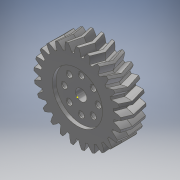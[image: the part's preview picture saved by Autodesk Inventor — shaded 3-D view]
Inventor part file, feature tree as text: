
AUTODESK INVENTOR PART (.ipt)
format: ipt  version: 2019 (Build 230136000, 136)  size: 762,368 bytes
history: native  units: mm (DEFAULTED — no unit token found)
features: sketch x7, extrude x4, plane x3, other x3, mirror x1, hole x1, chamfer x1
ambient origin geometry x8: Origin, YZ Plane, XZ Plane, XY Plane, X Axis, Y Axis, Z Axis, Center Point
bodies: Solid1 (feature_tree)
feature tree (20):
  extrude  "Extrusion1"  Depth=5.0mm TaperAngle=0.0deg
  plane  "Work Plane2"
  plane  "Work Plane8"
  plane  "Work Plane9"
  other  "Spur Gear"
  mirror  "Mirror1"
  extrude  "Extrusion13"  Depth=10.0mm TaperAngle=0.0deg
  sketch  "Sketch21"  dims[d39=0.0mm d41=0.0mm]
  extrude  "Extrusion15"  Depth=1.256637mm TaperAngle=0.0deg
  extrude  "Extrusion16"  TaperAngle=0.0deg  [1 undecoded]
  hole  "Hole4"  [1 undecoded]
  chamfer  "Chamfer2"  [1 undecoded]
  sketch  "Sketch1"  dims[d0=34.756617mm d1=5.0mm d2=0.0mm]
  sketch  "Sketch2"  dims[d3=32.258065mm d4=10.0mm d5=0.0mm]
  other  "Srf1"
  sketch  "Sketch19"  dims[d16=40.0mm d17=0.0mm d34=1.256637mm]
  sketch  "Sketch22"  dims[d43=40.0mm d46=40.0mm d47=0.0mm d48=0.0mm]
  sketch  "Sketch23"  dims[d126=4.5mm]
  sketch  "Sketch24"  dims[d127=10.0mm d128=0.0mm d132=20.0mm d133=1.5mm d134=0.0mm d135=18.0mm d136=5.0mm d137=0.0mm d138=13.5mm d139=80.0mm d141=360.0deg d143=2.5mm d144=6.0mm d145=4.0mm d146=3.0mm d147=90.0deg d148=10.0mm d149=0.0mm d150=1.5mm d151=4.0mm d152=45.0deg]
  other  "Pitch Diameter"
note: 3 required parameter values undecoded (feature->parameter linkage not recoverable at this tier; creation-order binding heuristic only, values carry confidence <= 0.55)
